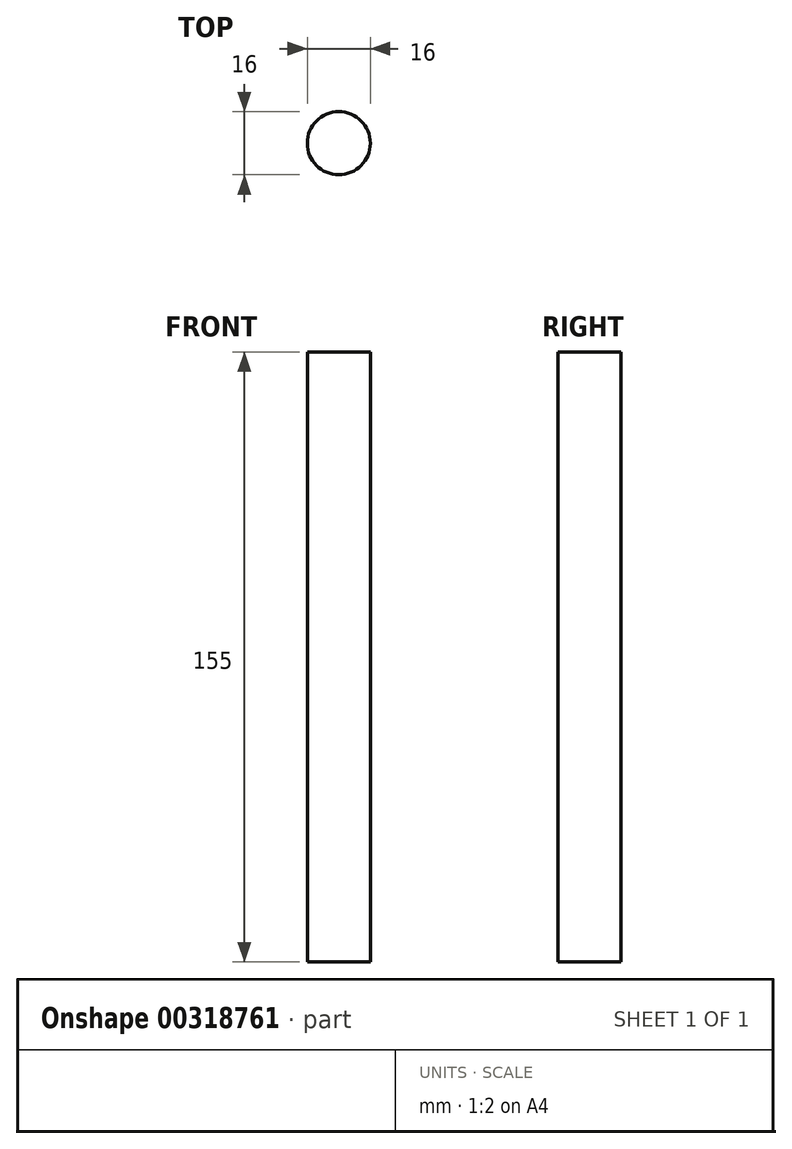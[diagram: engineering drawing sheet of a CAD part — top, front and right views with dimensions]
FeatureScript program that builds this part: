
annotation { "Feature Type Name" : "Feature", "Feature Type Description" : "" }
export const myFeature = defineFeature(function(context is Context, id is Id, definition is map)
    precondition{}
    {
        {
            var Q0;
            Q0=qCreatedBy(makeId("Top.planeOp"),FACE);
            var sketch = newSketch(context, id + "F0", { "sketchPlane" : qUnion([Q0])});
            skCircle(sketch, "E0", {"center": v(0, 0) * mm, "radius": 8 * mm});
            skSolve(sketch);
        }
        {
            var Q0;
            Q0 = qSketchRegion(id + "F0", true);
            extrude(context, id + "F1", {"entities" : qUnion([Q0]), "depth" : 155 * mm, "offsetDistance" : 25 * mm});
        }
    });
